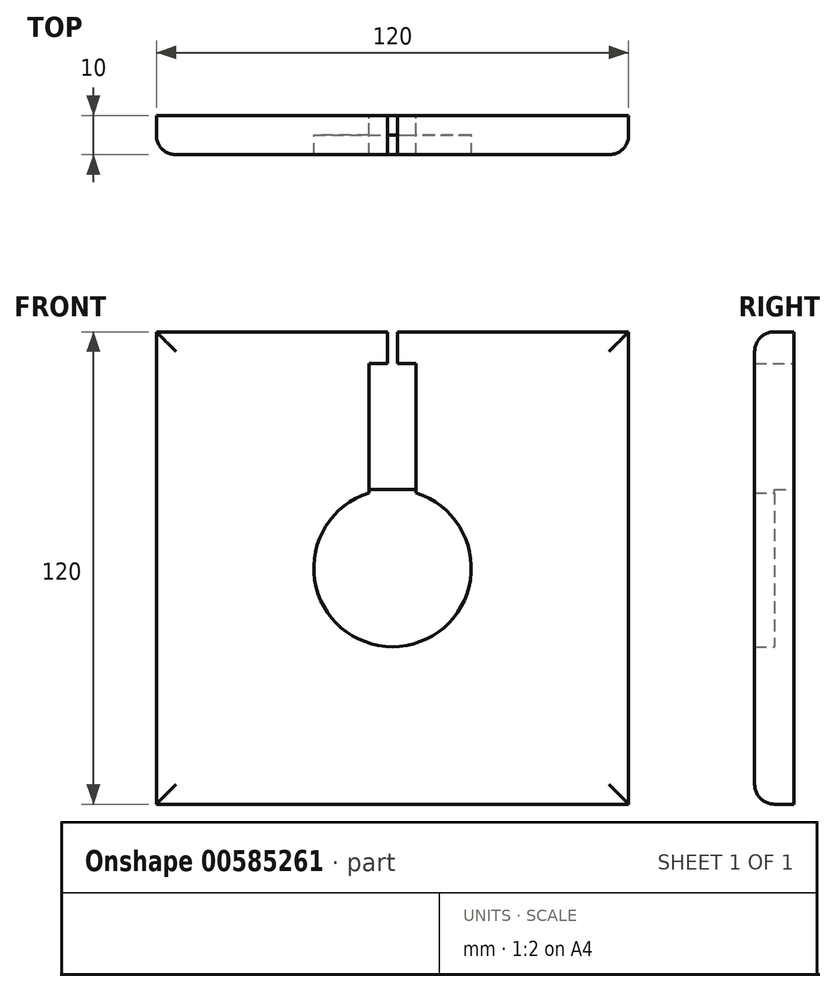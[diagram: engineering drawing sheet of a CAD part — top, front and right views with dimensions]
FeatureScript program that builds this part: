
annotation { "Feature Type Name" : "Feature", "Feature Type Description" : "" }
export const myFeature = defineFeature(function(context is Context, id is Id, definition is map)
    precondition{}
    {
        {
            var Q0;
            Q0=qCreatedBy(makeId("Front.planeOp"),FACE);
            var sketch = newSketch(context, id + "F0", { "sketchPlane" : qUnion([Q0])});
            skLineSegment(sketch, "E0.bottom", {"start": v(0, 0) * mm, "end": v(120, 0) * mm});
            skLineSegment(sketch, "E0.top", {"start": v(0, 120) * mm, "end": v(120, 120) * mm});
            skLineSegment(sketch, "E0.left", {"start": v(0, 0) * mm, "end": v(0, 120) * mm});
            skLineSegment(sketch, "E0.right", {"start": v(120, 0) * mm, "end": v(120, 120) * mm});
            skPoint(sketch, "E1", {"position": v(60, 60) * mm});
            skPoint(sketch, "E1.positionSnap0", {"position": v(60, 120) * mm});
            skPoint(sketch, "E1.positionSnap1", {"position": v(120, 60) * mm});
            skCircle(sketch, "E2", {"center": v(60, 60) * mm, "radius": 20 * mm});
            skLineSegment(sketch, "E3", {"start": v(60, 60) * mm, "end": v(54, 60) * mm});
            skLineSegment(sketch, "E4", {"start": v(60, 60) * mm, "end": v(66, 60) * mm});
            skLineSegment(sketch, "E5", {"start": v(66, 60) * mm, "end": v(66, 120) * mm});
            skLineSegment(sketch, "E6", {"start": v(54, 60) * mm, "end": v(54, 120) * mm});
            skLineSegment(sketch, "E7", {"start": v(54, 80) * mm, "end": v(66, 80) * mm});
            skLineSegment(sketch, "E8", {"start": v(66, 80) * mm, "end": v(66, 112) * mm});
            skLineSegment(sketch, "E9", {"start": v(66, 112) * mm, "end": v(61.25, 112) * mm});
            skLineSegment(sketch, "E10", {"start": v(54, 80) * mm, "end": v(54, 112) * mm});
            skLineSegment(sketch, "E11", {"start": v(54, 112) * mm, "end": v(58.75, 112) * mm});
            skLineSegment(sketch, "E12", {"start": v(58.75, 112) * mm, "end": v(58.75, 120) * mm});
            skLineSegment(sketch, "E13", {"start": v(61.25, 112) * mm, "end": v(61.25, 120) * mm});
            skLineSegment(sketch, "E14", {"start": v(58.75, 117.5) * mm, "end": v(61.25, 117.5) * mm});
            skSolve(sketch);
        }
        {
            var Q0;
            {var subQ4=sQuery(id+"F0.wireOp",EDGE,"E3");Q0=makeQuery(id+"F0.imprint","IMPRINT",FACE,{"disambiguationData":[TD([[makeQuery(id+"F0.imprint","IMPRINT",EDGE,{"derivedFrom":subQ4}),1.0]])]});}
            var Q1;
            {var subQ1=sQuery(id+"F0.wireOp",EDGE,"E3");Q1=makeQuery(id+"F0.imprint","IMPRINT",FACE,{"disambiguationData":[TD([[makeQuery(id+"F0.imprint","IMPRINT",EDGE,{"derivedFrom":subQ1}),-1.0]])]});}
            var Q2;
            {var subQ0=sQuery(id+"F0.wireOp",EDGE,"E7");var subQ1=sQuery(id+"F0.wireOp",EDGE,"E2");var subQ2=makeQuery(id+"F0.imprint","INTERSECT",VERTEX,{"derivedFrom":[subQ1,subQ0]});Q2=makeQuery(id+"F0.imprint","IMPRINT",FACE,{"disambiguationData":[TD([[makeQuery(id+"F0.imprint","IMPRINT",EDGE,{"disambiguationData":[TD([[subQ2,1.0]])],"derivedFrom":subQ1}),-1.0]])]});}
            var Q3;
            {var subQ0=sQuery(id+"F0.wireOp",EDGE,"E7");var subQ1=sQuery(id+"F0.wireOp",EDGE,"E2");var subQ2=makeQuery(id+"F0.imprint","INTERSECT",VERTEX,{"derivedFrom":[subQ1,subQ0]});Q3=makeQuery(id+"F0.imprint","IMPRINT",FACE,{"disambiguationData":[TD([[makeQuery(id+"F0.imprint","IMPRINT",EDGE,{"disambiguationData":[TD([[subQ2,-1.0]])],"derivedFrom":subQ1}),-1.0]])]});}
            var Q4;
            {var subQ1=sQuery(id+"F0.wireOp",EDGE,"E8");Q4=makeQuery(id+"F0.imprint","IMPRINT",FACE,{"disambiguationData":[TD([[makeQuery(id+"F0.imprint","IMPRINT",EDGE,{"derivedFrom":subQ1}),1.0]])]});}
            extrude(context, id + "F1", {"entities" : qUnion([Q0, Q1, Q2, Q3, Q4]), "depth" : 5 * mm, "offsetDistance" : 25 * mm});
        }
        {
            var Q0;
            Q0=makeQuery(id+"F0.imprint","IMPRINT",FACE,{"disambiguationData":[TD([[makeQuery(id+"F0.imprint","IMPRINT",EDGE,{"derivedFrom":sQuery(id+"F0.wireOp",EDGE,"E0.bottom")}),1.0]])]});
            var Q1;
            {var subQ1=sQuery(id+"F0.wireOp",EDGE,"E11");Q1=makeQuery(id+"F0.imprint","IMPRINT",FACE,{"disambiguationData":[TD([[makeQuery(id+"F0.imprint","IMPRINT",EDGE,{"derivedFrom":subQ1}),1.0]])]});}
            var Q2;
            {var subQ1=sQuery(id+"F0.wireOp",EDGE,"E9");Q2=makeQuery(id+"F0.imprint","IMPRINT",FACE,{"disambiguationData":[TD([[makeQuery(id+"F0.imprint","IMPRINT",EDGE,{"derivedFrom":subQ1}),-1.0]])]});}
            extrude(context, id + "F2", {"entities" : qUnion([Q0, Q1, Q2]), "operationType" : NewBodyOperationType.ADD, "depth" : 10 * mm, "offsetDistance" : 25 * mm});
        }
        {
            var Q0;
            Q0=makeQuery(id+"F2.opExtrude","CAP_EDGE",EDGE,{"disambiguationData":[OSD([sQuery(id+"F0.wireOp",EDGE,"E0.left")])],"isStart":false});
            var Q1;
            Q1=makeQuery(id+"F2.opExtrude","CAP_EDGE",EDGE,{"disambiguationData":[OSD([sQuery(id+"F0.wireOp",EDGE,"E0.bottom")])],"isStart":false});
            var Q2;
            Q2=makeQuery(id+"F2.opExtrude","CAP_EDGE",EDGE,{"disambiguationData":[OSD([sQuery(id+"F0.wireOp",EDGE,"E0.right")])],"isStart":false});
            var Q3;
            {var subQ0=sQuery(id+"F0.wireOp",EDGE,"E0.top");var subQ1=makeQuery(id+"F0.imprint","INTERSECT",VERTEX,{"derivedFrom":[subQ0,sQuery(id+"F0.wireOp",EDGE,"E5")]});Q3=makeQuery(id+"F2.opExtrude","CAP_EDGE",EDGE,{"disambiguationData":[OSD([subQ0]),TDD([makeQuery(id+"F0.imprint","IMPRINT",EDGE,{"disambiguationData":[TD([[subQ1,1.0]])],"derivedFrom":subQ0}),makeQuery(id+"F0.imprint","IMPRINT",EDGE,{"disambiguationData":[TD([[makeQuery(id+"F0.imprint","INTERSECT",VERTEX,{"derivedFrom":[subQ0,sQuery(id+"F0.wireOp",EDGE,"E0.right")]}),1.0]])],"derivedFrom":subQ0})])],"isStart":false});}
            var Q4;
            {var subQ0=sQuery(id+"F0.wireOp",EDGE,"E0.top");var subQ1=makeQuery(id+"F0.imprint","INTERSECT",VERTEX,{"derivedFrom":[subQ0,sQuery(id+"F0.wireOp",EDGE,"E6")]});Q4=makeQuery(id+"F2.opExtrude","CAP_EDGE",EDGE,{"disambiguationData":[OSD([subQ0]),TDD([makeQuery(id+"F0.imprint","IMPRINT",EDGE,{"disambiguationData":[TD([[makeQuery(id+"F0.imprint","INTERSECT",VERTEX,{"derivedFrom":[subQ0,sQuery(id+"F0.wireOp",EDGE,"E0.left")]}),-1.0]])],"derivedFrom":subQ0}),makeQuery(id+"F0.imprint","IMPRINT",EDGE,{"disambiguationData":[TD([[subQ1,-1.0]])],"derivedFrom":subQ0})])],"isStart":false});}
            fillet(context, id + "F3", {"entities" : qUnion([Q0, Q1, Q2, Q3, Q4]), "radius" : 5 * mm, "tangentPropagation" : true, "allowEdgeOverflow" : false});
        }
    });
